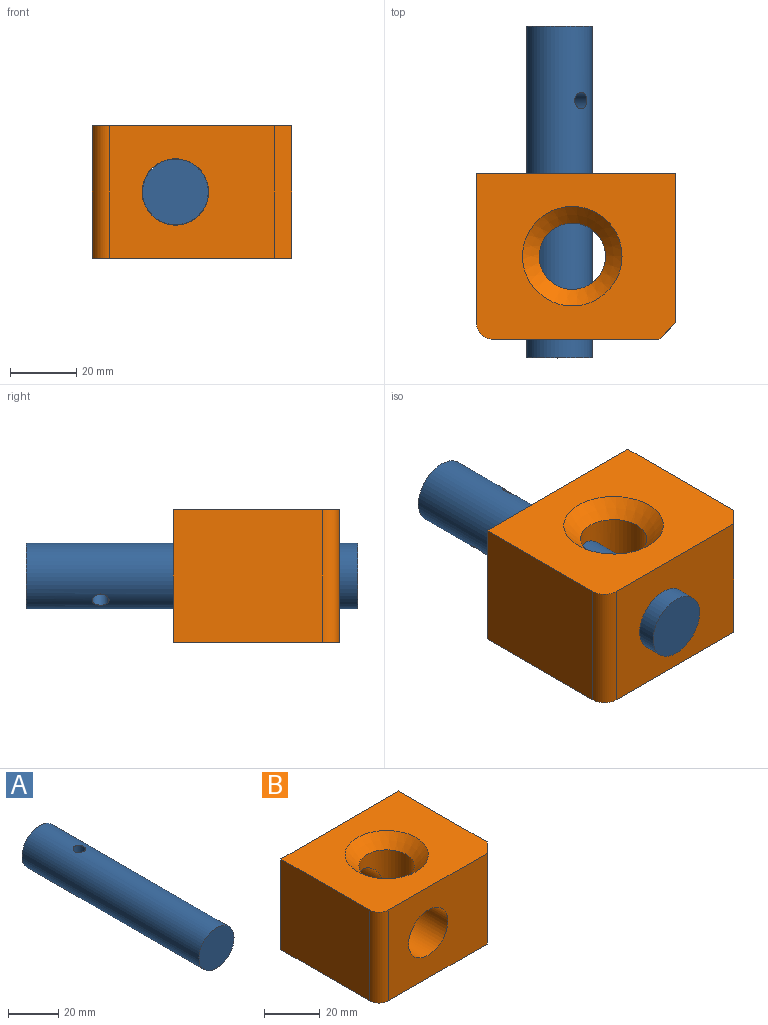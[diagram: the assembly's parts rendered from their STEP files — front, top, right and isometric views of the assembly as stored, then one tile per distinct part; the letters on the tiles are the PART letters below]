
ASSEMBLY  parts=2 mates=1
PART A: 4 faces, bbox 19.8x100x19.8 mm
  f0: cylinder r=9.9mm len=100mm, axis (0,1,0), area 6180.8mm2, adj f1,f2,f3
  f1: plane 19.8x19.8mm, normal (0,-1,0), area 307.9mm2, adj f0
  f2: plane 19.8x19.8mm, normal (0,1,0), area 307.9mm2, adj f0
  f3: cylinder r=2.5mm len=19.8mm, axis (0,0,1), area 306mm2, adj f0
PART B: 12 faces, bbox 60x50x40 mm
  f0: plane 45x40mm, normal (-1,0,0), area 1800mm2, adj f1,f3,f5,f7
  f1: plane 60x50mm, normal (0,0,-1), area 2275.3mm2, adj f0,f2,f4,f5,f7,f8,f10
  f2: plane 45x40mm, normal (1,0,0), area 1800mm2, adj f1,f3,f5,f8
  f3: plane 60x50mm, normal (0,0,1), area 2275.3mm2, adj f0,f2,f4,f5,f7,f8,f9
  f4: plane 50x40mm, normal (0,-1,0), area 1685.8mm2, adj f1,f3,f7,f8,f11
  f5: plane 60x40mm, normal (0,1,0), area 2085.8mm2, adj f0,f1,f2,f3,f11
  f6: cylinder r=10mm len=30mm, axis (0,0,1), area 1138.3mm2, adj f9,f10,f11
  f7: cylinder r=5mm len=40mm, axis (0,0,1), area 314.2mm2, adj f0,f1,f3,f4
  f8: plane 40x5mm, normal (0.71,-0.71,0), area 282.8mm2, adj f1,f2,f3,f4
  f9: cone r=10mm half-angle=45deg, axis (0,0,1), area 555.4mm2, adj f3,f6
  f10: torus R=15mm, axis (0,0,1), area 583.1mm2, adj f1,f6
  f11: cylinder r=10mm len=50mm, axis (0,-1,0), area 2394.7mm2, adj f4,f5,f6
PLACE A rot(axis=(0,-1,0),137.8deg) t=(-1.24,99.03,24.31)mm
PLACE B t=(-26.24,54.65,4.31)mm fixed
MATE cylindrical A.f0 <-> B.f11  axis (0,1,0) through (-1.24,49.03,24.31)mm
